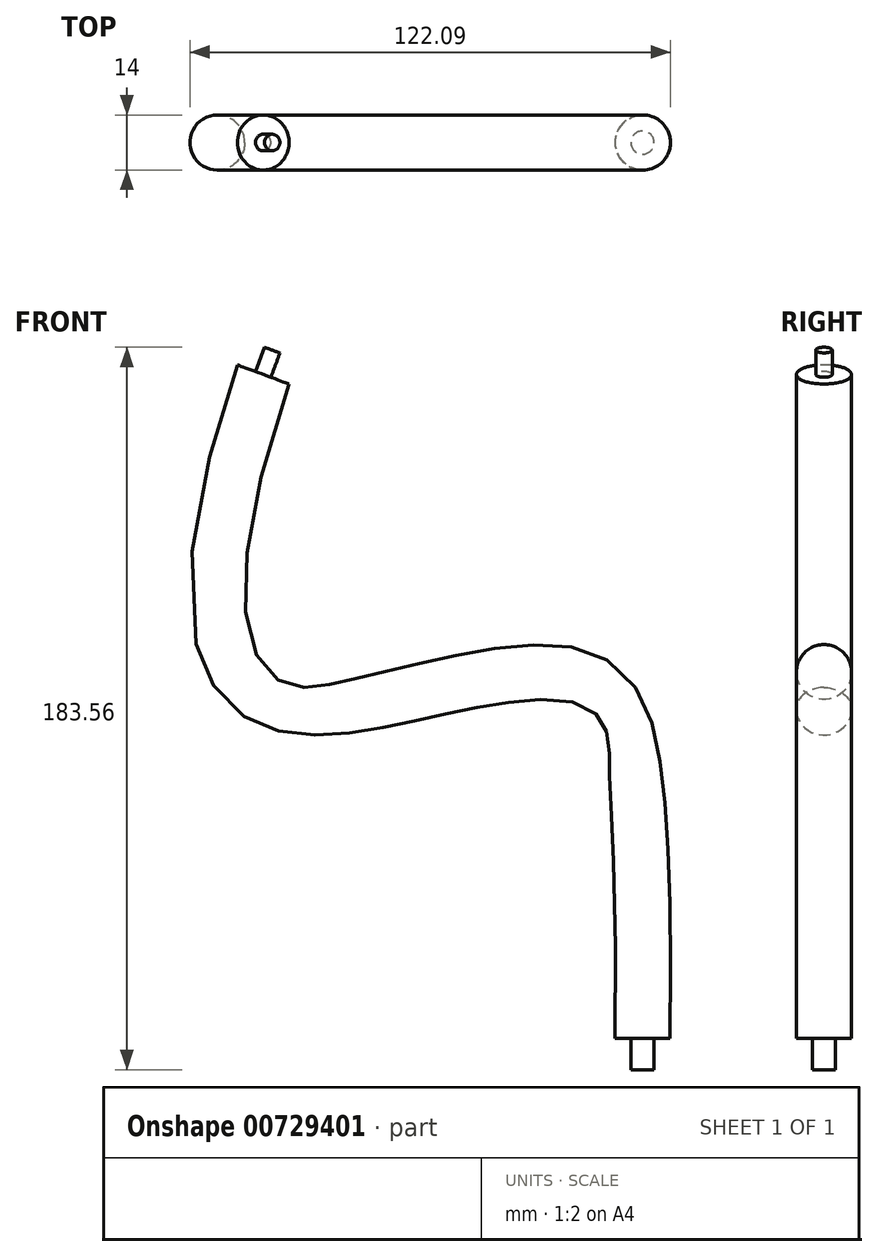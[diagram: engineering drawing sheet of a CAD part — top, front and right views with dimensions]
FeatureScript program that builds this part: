
annotation { "Feature Type Name" : "Feature", "Feature Type Description" : "" }
export const myFeature = defineFeature(function(context is Context, id is Id, definition is map)
    precondition{}
    {
        {
            var Q0;
            Q0=qCreatedBy(makeId("Front.planeOp"),FACE);
            var sketch = newSketch(context, id + "F0", { "sketchPlane" : qUnion([Q0])});
            skFitSpline(sketch, "E0", {"points": [v(0, 12) * mm, v(-20.92, 91.4) * mm, v(-82.41, 85.95) * mm, v(-92.23, 180) * mm], "startDerivative": vector(0, 448.28) * mm, "endDerivative": vector(221, 598.36) * mm});
            skLineSegment(sketch, "E1", {"start": v(0, 0) * mm, "end": v(0, 12) * mm});
            skLineSegment(sketch, "E2", {"start": v(-92.23, 180) * mm, "end": v(-85.3, 198.76) * mm});
            skSolve(sketch);
        }
        {
            var Q0;
            Q0=qCreatedBy(makeId("Top.planeOp"),FACE);
            var sketch = newSketch(context, id + "F1", { "sketchPlane" : qUnion([Q0])});
            skCircle(sketch, "E3", {"center": v(0, 0) * mm, "radius": 7 * mm});
            skSolve(sketch);
        }
        {
            var Q0;
            Q0=makeQuery(id+"F1.imprint","IMPRINT",FACE,{"disambiguationData":[TD([[makeQuery(id+"F1.imprint","IMPRINT",EDGE,{"derivedFrom":sQuery(id+"F1.wireOp",EDGE,"E3")}),1.0]])]});
            var Q1;
            Q1=sQuery(id+"F0.wireOp",EDGE,"E0");
            sweep(context, id + "F2", {"profiles" : qUnion([Q0]), "path" : qUnion([Q1])});
        }
        {
            var Q0;
            Q0=makeQuery(id+"F2.opSweep","CAP_FACE",FACE,{"disambiguationData":[OSD([sQuery(id+"F0.wireOp",VERTEX,"E0.start"),sQuery(id+"F1.wireOp",EDGE,"E3")])],"isStart":true});
            var sketch = newSketch(context, id + "F3", { "sketchPlane" : qUnion([Q0])});
            skCircle(sketch, "E4", {"center": v(0, 0) * mm, "radius": 2.95 * mm});
            skSolve(sketch);
        }
        {
            var Q0;
            Q0=makeQuery(id+"F3.imprint","IMPRINT",FACE,{"disambiguationData":[TD([[makeQuery(id+"F3.imprint","IMPRINT",EDGE,{"derivedFrom":sQuery(id+"F3.wireOp",EDGE,"E4")}),1.0]])]});
            extrude(context, id + "F4", {"entities" : qUnion([Q0]), "operationType" : NewBodyOperationType.ADD, "depth" : 7.9 * mm, "offsetDistance" : 25 * mm});
        }
        {
            var Q0;
            Q0=makeQuery(id+"F2.opSweep","CAP_FACE",FACE,{"disambiguationData":[OSD([sQuery(id+"F0.wireOp",VERTEX,"E0.end"),sQuery(id+"F1.wireOp",EDGE,"E3")])],"isStart":false});
            var sketch = newSketch(context, id + "F5", { "sketchPlane" : qUnion([Q0])});
            skCircle(sketch, "E5.0", {"center": v(-148.88, 0) * mm, "radius": 2.1 * mm});
            skSolve(sketch);
        }
        {
            var Q0;
            Q0=makeQuery(id+"F5.imprint","IMPRINT",FACE,{"disambiguationData":[TD([[makeQuery(id+"F5.imprint","IMPRINT",EDGE,{"derivedFrom":sQuery(id+"F5.wireOp",EDGE,"E5.0")}),1.0]])]});
            extrude(context, id + "F6", {"entities" : qUnion([Q0]), "operationType" : NewBodyOperationType.ADD, "depth" : 6.6 * mm, "offsetDistance" : 25 * mm});
        }
    });
